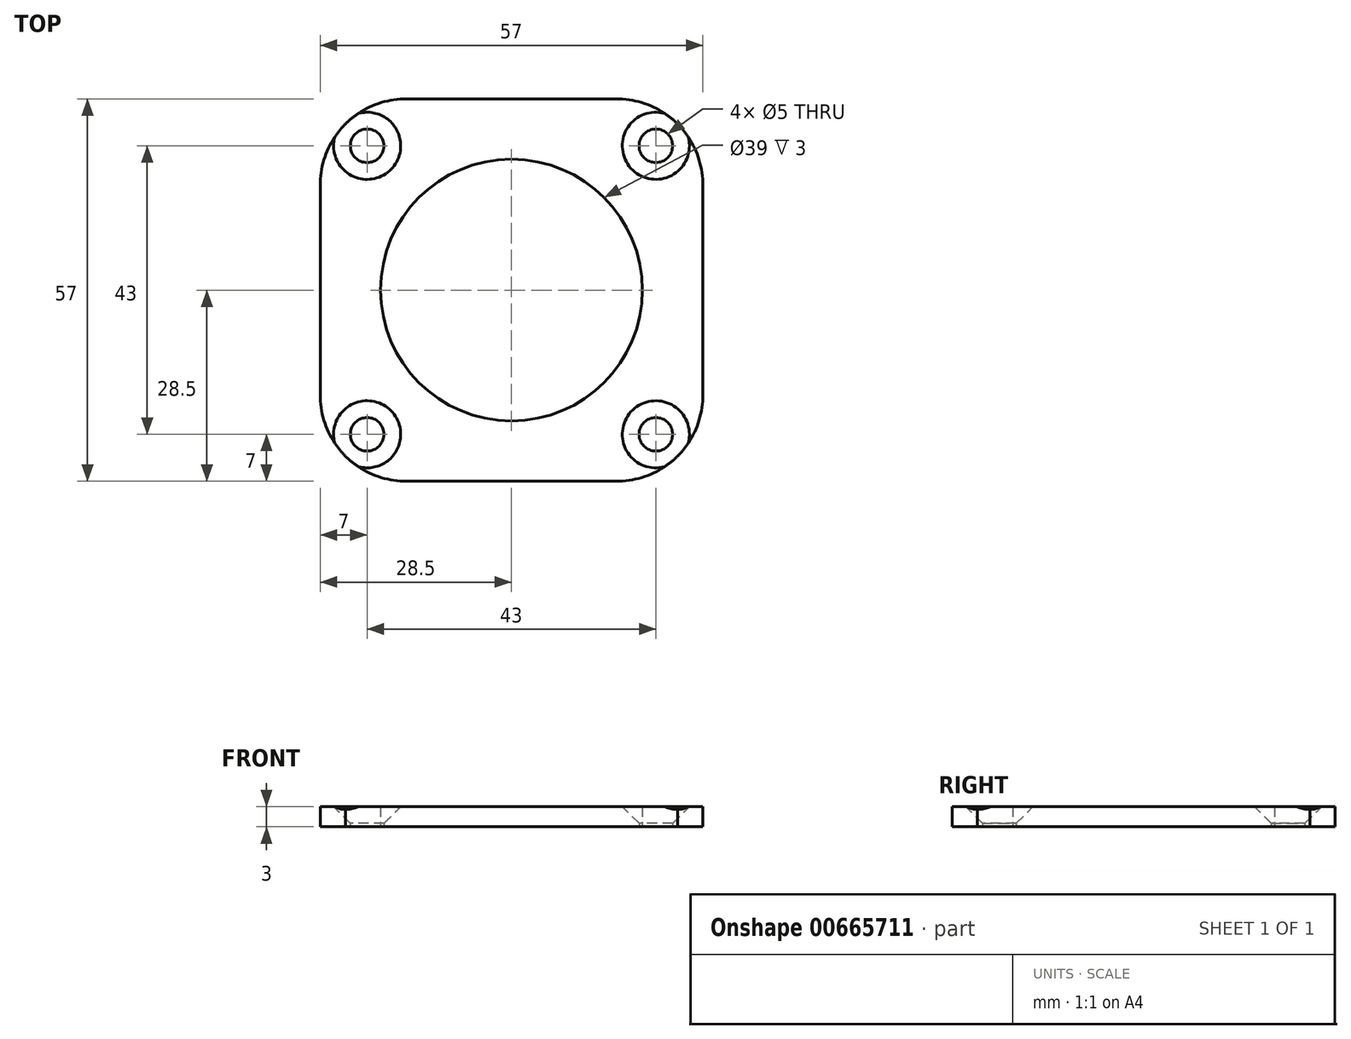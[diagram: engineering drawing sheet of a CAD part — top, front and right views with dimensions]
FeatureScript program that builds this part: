
annotation { "Feature Type Name" : "Feature", "Feature Type Description" : "" }
export const myFeature = defineFeature(function(context is Context, id is Id, definition is map)
    precondition{}
    {
        {
            var Q0;
            Q0=qCreatedBy(makeId("Top.planeOp"),FACE);
            var sketch = newSketch(context, id + "F0", { "sketchPlane" : qUnion([Q0])});
            skCircle(sketch, "E0", {"center": v(0, 0) * mm, "radius": 12.5 * mm});
            skCircle(sketch, "E1", {"center": v(0, 0) * mm, "radius": 23.5 * mm});
            skLineSegment(sketch, "E2.bottom", {"start": v(28.5, -28.5) * mm, "end": v(-28.5, -28.5) * mm});
            skLineSegment(sketch, "E2.top", {"start": v(28.5, 28.5) * mm, "end": v(-28.5, 28.5) * mm});
            skLineSegment(sketch, "E2.left", {"start": v(28.5, -28.5) * mm, "end": v(28.5, 28.5) * mm});
            skLineSegment(sketch, "E2.right", {"start": v(-28.5, -28.5) * mm, "end": v(-28.5, 28.5) * mm});
            skCircle(sketch, "E3", {"center": v(0, 0) * mm, "radius": 19.5 * mm});
            skCircle(sketch, "E4", {"center": v(0, 0) * mm, "radius": 15 * mm});
            skLineSegment(sketch, "E5.bottom", {"start": v(-21.5, 21.5) * mm, "end": v(21.5, 21.5) * mm, "construction": true});
            skLineSegment(sketch, "E5.top", {"start": v(-21.5, -21.5) * mm, "end": v(21.5, -21.5) * mm, "construction": true});
            skLineSegment(sketch, "E5.left", {"start": v(-21.5, 21.5) * mm, "end": v(-21.5, -21.5) * mm, "construction": true});
            skLineSegment(sketch, "E5.right", {"start": v(21.5, 21.5) * mm, "end": v(21.5, -21.5) * mm, "construction": true});
            skCircle(sketch, "E6", {"center": v(-21.5, 21.5) * mm, "radius": 2.5 * mm});
            skCircle(sketch, "E7", {"center": v(21.5, 21.5) * mm, "radius": 2.5 * mm});
            skCircle(sketch, "E8", {"center": v(21.5, -21.5) * mm, "radius": 2.5 * mm});
            skCircle(sketch, "E9", {"center": v(-21.5, -21.5) * mm, "radius": 2.5 * mm});
            skCircle(sketch, "E10", {"center": v(0, 0) * mm, "radius": 35 * mm});
            skSolve(sketch);
        }
        {
            var Q0;
            Q0=makeQuery(id+"F0.imprint","IMPRINT",FACE,{"disambiguationData":[TD([[makeQuery(id+"F0.imprint","IMPRINT",EDGE,{"derivedFrom":sQuery(id+"F0.wireOp",EDGE,"E1")}),1.0]])]});
            var Q1;
            Q1=makeQuery(id+"F0.imprint","IMPRINT",FACE,{"disambiguationData":[TD([[makeQuery(id+"F0.imprint","IMPRINT",EDGE,{"derivedFrom":sQuery(id+"F0.wireOp",EDGE,"E1")}),-1.0]])]});
            extrude(context, id + "F1", {"entities" : qUnion([Q0, Q1]), "depth" : 3 * mm, "offsetDistance" : 25 * mm});
        }
        {
            var Q0;
            Q0=makeQuery(id+"F0.imprint","IMPRINT",FACE,{"disambiguationData":[TD([[makeQuery(id+"F0.imprint","IMPRINT",EDGE,{"derivedFrom":sQuery(id+"F0.wireOp",EDGE,"E1")}),1.0]])]});
            extrude(context, id + "F2", {"entities" : qUnion([Q0]), "operationType" : NewBodyOperationType.ADD, "depth" : 2.5 * mm, "offsetDistance" : 25 * mm});
        }
        {
            var Q0;
            {var subQ0=sQuery(id+"F0.wireOp",EDGE,"E10");var subQ1=sQuery(id+"F0.wireOp",EDGE,"E2.right");Q0=makeQuery(id+"F1.opExtrude","SWEPT_EDGE",EDGE,{"disambiguationData":[OSD([subQ1,subQ0]),TDD([makeQuery(id+"F0.imprint","INTERSECT",VERTEX,{"disambiguationData":[OD(1.0)],"derivedFrom":[subQ1,subQ0]})])]});}
            var Q1;
            {var subQ0=sQuery(id+"F0.wireOp",EDGE,"E10");var subQ1=sQuery(id+"F0.wireOp",EDGE,"E2.top");Q1=makeQuery(id+"F1.opExtrude","SWEPT_EDGE",EDGE,{"disambiguationData":[OSD([subQ1,subQ0]),TDD([makeQuery(id+"F0.imprint","INTERSECT",VERTEX,{"disambiguationData":[OD(1.0)],"derivedFrom":[subQ1,subQ0]})])]});}
            var Q2;
            {var subQ0=sQuery(id+"F0.wireOp",EDGE,"E10");var subQ1=sQuery(id+"F0.wireOp",EDGE,"E2.top");Q2=makeQuery(id+"F1.opExtrude","SWEPT_EDGE",EDGE,{"disambiguationData":[OSD([subQ1,subQ0]),TDD([makeQuery(id+"F0.imprint","INTERSECT",VERTEX,{"disambiguationData":[OD(0.0)],"derivedFrom":[subQ1,subQ0]})])]});}
            var Q3;
            {var subQ0=sQuery(id+"F0.wireOp",EDGE,"E10");var subQ1=sQuery(id+"F0.wireOp",EDGE,"E2.left");Q3=makeQuery(id+"F1.opExtrude","SWEPT_EDGE",EDGE,{"disambiguationData":[OSD([subQ1,subQ0]),TDD([makeQuery(id+"F0.imprint","INTERSECT",VERTEX,{"disambiguationData":[OD(1.0)],"derivedFrom":[subQ1,subQ0]})])]});}
            var Q4;
            {var subQ0=sQuery(id+"F0.wireOp",EDGE,"E10");var subQ1=sQuery(id+"F0.wireOp",EDGE,"E2.left");Q4=makeQuery(id+"F1.opExtrude","SWEPT_EDGE",EDGE,{"disambiguationData":[OSD([subQ1,subQ0]),TDD([makeQuery(id+"F0.imprint","INTERSECT",VERTEX,{"disambiguationData":[OD(0.0)],"derivedFrom":[subQ1,subQ0]})])]});}
            var Q5;
            {var subQ0=sQuery(id+"F0.wireOp",EDGE,"E10");var subQ1=sQuery(id+"F0.wireOp",EDGE,"E2.bottom");Q5=makeQuery(id+"F1.opExtrude","SWEPT_EDGE",EDGE,{"disambiguationData":[OSD([subQ1,subQ0]),TDD([makeQuery(id+"F0.imprint","INTERSECT",VERTEX,{"disambiguationData":[OD(0.0)],"derivedFrom":[subQ1,subQ0]})])]});}
            var Q6;
            {var subQ0=sQuery(id+"F0.wireOp",EDGE,"E10");var subQ1=sQuery(id+"F0.wireOp",EDGE,"E2.bottom");Q6=makeQuery(id+"F1.opExtrude","SWEPT_EDGE",EDGE,{"disambiguationData":[OSD([subQ1,subQ0]),TDD([makeQuery(id+"F0.imprint","INTERSECT",VERTEX,{"disambiguationData":[OD(1.0)],"derivedFrom":[subQ1,subQ0]})])]});}
            var Q7;
            {var subQ0=sQuery(id+"F0.wireOp",EDGE,"E10");var subQ1=sQuery(id+"F0.wireOp",EDGE,"E2.right");Q7=makeQuery(id+"F1.opExtrude","SWEPT_EDGE",EDGE,{"disambiguationData":[OSD([subQ1,subQ0]),TDD([makeQuery(id+"F0.imprint","INTERSECT",VERTEX,{"disambiguationData":[OD(0.0)],"derivedFrom":[subQ1,subQ0]})])]});}
            fillet(context, id + "F3", {"entities" : qUnion([Q0, Q1, Q2, Q3, Q4, Q5, Q6, Q7]), "radius" : 13 * mm, "tangentPropagation" : true, "allowEdgeOverflow" : false});
        }
        {
            var Q0;
            Q0=makeQuery(id+"F1.opExtrude","CAP_EDGE",EDGE,{"disambiguationData":[OSD([sQuery(id+"F0.wireOp",EDGE,"E6")])],"isStart":false});
            var Q1;
            Q1=makeQuery(id+"F1.opExtrude","CAP_EDGE",EDGE,{"disambiguationData":[OSD([sQuery(id+"F0.wireOp",EDGE,"E7")])],"isStart":false});
            var Q2;
            Q2=makeQuery(id+"F1.opExtrude","CAP_EDGE",EDGE,{"disambiguationData":[OSD([sQuery(id+"F0.wireOp",EDGE,"E8")])],"isStart":false});
            var Q3;
            Q3=makeQuery(id+"F1.opExtrude","CAP_EDGE",EDGE,{"disambiguationData":[OSD([sQuery(id+"F0.wireOp",EDGE,"E9")])],"isStart":false});
            chamfer(context, id + "F4", {"entities" : qUnion([Q0, Q1, Q2, Q3]), "width" : 2.5 * mm, "tangentPropagation" : true});
        }
    });
